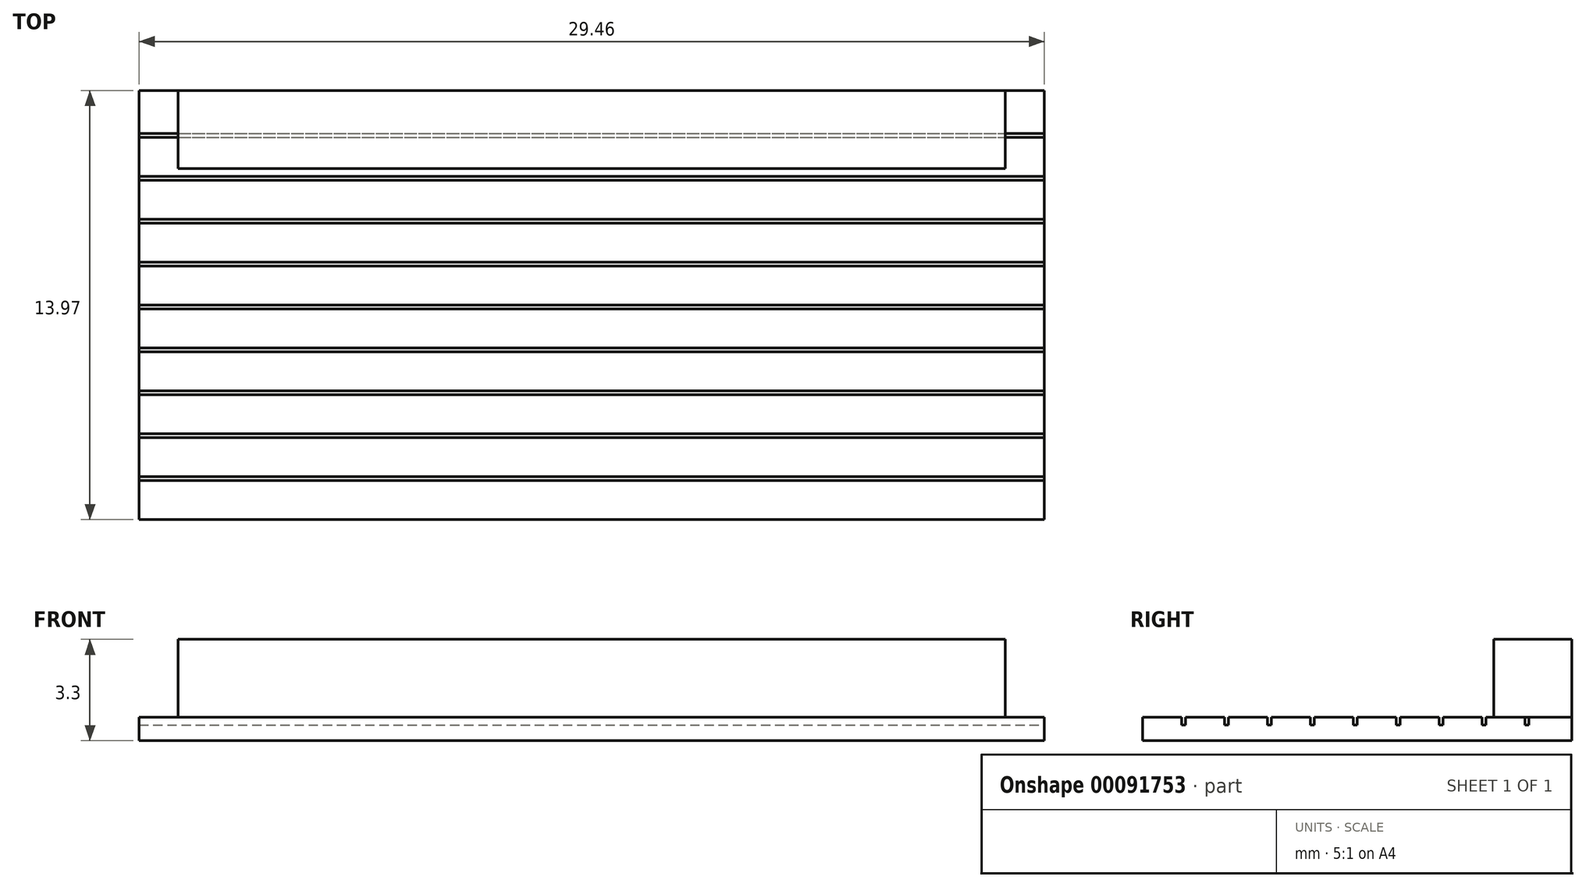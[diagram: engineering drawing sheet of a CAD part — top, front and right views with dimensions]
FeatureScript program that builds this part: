
annotation { "Feature Type Name" : "Feature", "Feature Type Description" : "" }
export const myFeature = defineFeature(function(context is Context, id is Id, definition is map)
    precondition{}
    {
        {
            var Q0;
            Q0=qCreatedBy(makeId("Top.planeOp"),FACE);
            var sketch = newSketch(context, id + "F0", { "sketchPlane" : qUnion([Q0])});
            skLineSegment(sketch, "E0.bottom", {"start": v(-13.46, 0) * mm, "end": v(13.46, 0) * mm});
            skLineSegment(sketch, "E0.top", {"start": v(-13.46, -2.54) * mm, "end": v(13.46, -2.54) * mm});
            skLineSegment(sketch, "E0.left", {"start": v(-13.46, 0) * mm, "end": v(-13.46, -2.54) * mm});
            skLineSegment(sketch, "E0.right", {"start": v(13.46, 0) * mm, "end": v(13.46, -2.54) * mm});
            skSolve(sketch);
        }
        {
            var Q0;
            Q0 = qSketchRegion(id + "F0", true);
            extrude(context, id + "F1", {"entities" : qUnion([Q0]), "depth" : 2.54 * mm});
        }
        {
            var Q0;
            Q0=qCreatedBy(makeId("Top.planeOp"),FACE);
            var sketch = newSketch(context, id + "F2", { "sketchPlane" : qUnion([Q0])});
            skLineSegment(sketch, "E1.bottom", {"start": v(-14.73, 0) * mm, "end": v(14.73, 0) * mm});
            skLineSegment(sketch, "E1.top", {"start": v(-14.73, -13.97) * mm, "end": v(14.73, -13.97) * mm});
            skLineSegment(sketch, "E1.left", {"start": v(-14.73, 0) * mm, "end": v(-14.73, -13.97) * mm});
            skLineSegment(sketch, "E1.right", {"start": v(14.73, 0) * mm, "end": v(14.73, -13.97) * mm});
            skSolve(sketch);
        }
        {
            var Q0;
            Q0 = qSketchRegion(id + "F2", true);
            extrude(context, id + "F3", {"entities" : qUnion([Q0]), "operationType" : NewBodyOperationType.ADD, "oppositeDirection" : true, "depth" : 0.76 * mm});
        }
        {
            var Q0;
            Q0=makeQuery(id+"F3.opExtrude","CAP_FACE",FACE,{"disambiguationData":[OSD([sQuery(id+"F2.wireOp",EDGE,"E1.bottom"),sQuery(id+"F2.wireOp",EDGE,"E1.top"),sQuery(id+"F2.wireOp",EDGE,"E1.left"),sQuery(id+"F2.wireOp",EDGE,"E1.right")])],"isStart":true});
            var sketch = newSketch(context, id + "F4", { "sketchPlane" : qUnion([Q0])});
            skLineSegment(sketch, "E2.bottom", {"start": v(-14.73, -12.7) * mm, "end": v(14.73, -12.7) * mm});
            skLineSegment(sketch, "E2.top", {"start": v(-14.73, -12.57) * mm, "end": v(14.73, -12.57) * mm});
            skLineSegment(sketch, "E2.left", {"start": v(-14.73, -12.7) * mm, "end": v(-14.73, -12.57) * mm});
            skLineSegment(sketch, "E2.right", {"start": v(14.73, -12.7) * mm, "end": v(14.73, -12.57) * mm});
            skLineSegment(sketch, "E3.0.1.0", {"start": v(-14.73, -11.18) * mm, "end": v(14.73, -11.18) * mm});
            skLineSegment(sketch, "E3.0.1.1", {"start": v(-14.73, -11.3) * mm, "end": v(14.73, -11.3) * mm});
            skLineSegment(sketch, "E3.0.1.2", {"start": v(14.73, -11.3) * mm, "end": v(14.73, -11.18) * mm});
            skLineSegment(sketch, "E3.0.1.3", {"start": v(-14.73, -11.3) * mm, "end": v(-14.73, -11.18) * mm});
            skLineSegment(sketch, "E3.0.2.0", {"start": v(-14.73, -9.78) * mm, "end": v(14.73, -9.78) * mm});
            skLineSegment(sketch, "E3.0.2.1", {"start": v(-14.73, -9.9) * mm, "end": v(14.73, -9.9) * mm});
            skLineSegment(sketch, "E3.0.2.2", {"start": v(14.73, -9.9) * mm, "end": v(14.73, -9.78) * mm});
            skLineSegment(sketch, "E3.0.2.3", {"start": v(-14.73, -9.9) * mm, "end": v(-14.73, -9.78) * mm});
            skLineSegment(sketch, "E3.0.3.0", {"start": v(-14.73, -8.38) * mm, "end": v(14.73, -8.38) * mm});
            skLineSegment(sketch, "E3.0.3.1", {"start": v(-14.73, -8.5) * mm, "end": v(14.73, -8.5) * mm});
            skLineSegment(sketch, "E3.0.3.2", {"start": v(14.73, -8.5) * mm, "end": v(14.73, -8.38) * mm});
            skLineSegment(sketch, "E3.0.3.3", {"start": v(-14.73, -8.5) * mm, "end": v(-14.73, -8.38) * mm});
            skLineSegment(sketch, "E3.0.4.0", {"start": v(-14.73, -6.99) * mm, "end": v(14.73, -6.98) * mm});
            skLineSegment(sketch, "E3.0.4.1", {"start": v(-14.73, -7.11) * mm, "end": v(14.73, -7.11) * mm});
            skLineSegment(sketch, "E3.0.4.2", {"start": v(14.73, -7.11) * mm, "end": v(14.73, -6.98) * mm});
            skLineSegment(sketch, "E3.0.4.3", {"start": v(-14.73, -7.11) * mm, "end": v(-14.73, -6.99) * mm});
            skLineSegment(sketch, "E3.0.5.0", {"start": v(-14.73, -5.59) * mm, "end": v(14.73, -5.59) * mm});
            skLineSegment(sketch, "E3.0.5.1", {"start": v(-14.73, -5.72) * mm, "end": v(14.73, -5.71) * mm});
            skLineSegment(sketch, "E3.0.5.2", {"start": v(14.73, -5.71) * mm, "end": v(14.73, -5.59) * mm});
            skLineSegment(sketch, "E3.0.5.3", {"start": v(-14.73, -5.72) * mm, "end": v(-14.73, -5.59) * mm});
            skLineSegment(sketch, "E3.0.6.0", {"start": v(-14.73, -4.2) * mm, "end": v(14.73, -4.2) * mm});
            skLineSegment(sketch, "E3.0.6.1", {"start": v(-14.73, -4.32) * mm, "end": v(14.73, -4.32) * mm});
            skLineSegment(sketch, "E3.0.6.2", {"start": v(14.73, -4.32) * mm, "end": v(14.73, -4.2) * mm});
            skLineSegment(sketch, "E3.0.6.3", {"start": v(-14.73, -4.32) * mm, "end": v(-14.73, -4.2) * mm});
            skLineSegment(sketch, "E3.0.7.0", {"start": v(-14.73, -2.8) * mm, "end": v(14.73, -2.8) * mm});
            skLineSegment(sketch, "E3.0.7.1", {"start": v(-14.73, -2.92) * mm, "end": v(14.73, -2.92) * mm});
            skLineSegment(sketch, "E3.0.7.2", {"start": v(14.73, -2.92) * mm, "end": v(14.73, -2.8) * mm});
            skLineSegment(sketch, "E3.0.7.3", {"start": v(-14.73, -2.92) * mm, "end": v(-14.73, -2.8) * mm});
            skLineSegment(sketch, "E3.0.8.0", {"start": v(-14.73, -1.4) * mm, "end": v(14.73, -1.4) * mm});
            skLineSegment(sketch, "E3.0.8.1", {"start": v(-14.73, -1.52) * mm, "end": v(14.73, -1.52) * mm});
            skLineSegment(sketch, "E3.0.8.2", {"start": v(14.73, -1.52) * mm, "end": v(14.73, -1.4) * mm});
            skLineSegment(sketch, "E3.0.8.3", {"start": v(-14.73, -1.52) * mm, "end": v(-14.73, -1.4) * mm});
            skLineSegment(sketch, "E3.direction1", {"start": v(-14.73, -12.07) * mm, "end": v(10.67, -12.07) * mm, "construction": true});
            skLineSegment(sketch, "E3.direction2", {"start": v(-14.73, -12.07) * mm, "end": v(-14.73, -10.67) * mm, "construction": true});
            skSolve(sketch);
        }
        {
            var Q0;
            Q0 = qSketchRegion(id + "F4", true);
            extrude(context, id + "F5", {"entities" : qUnion([Q0]), "operationType" : NewBodyOperationType.REMOVE, "oppositeDirection" : true, "depth" : 0.25 * mm});
        }
    });
